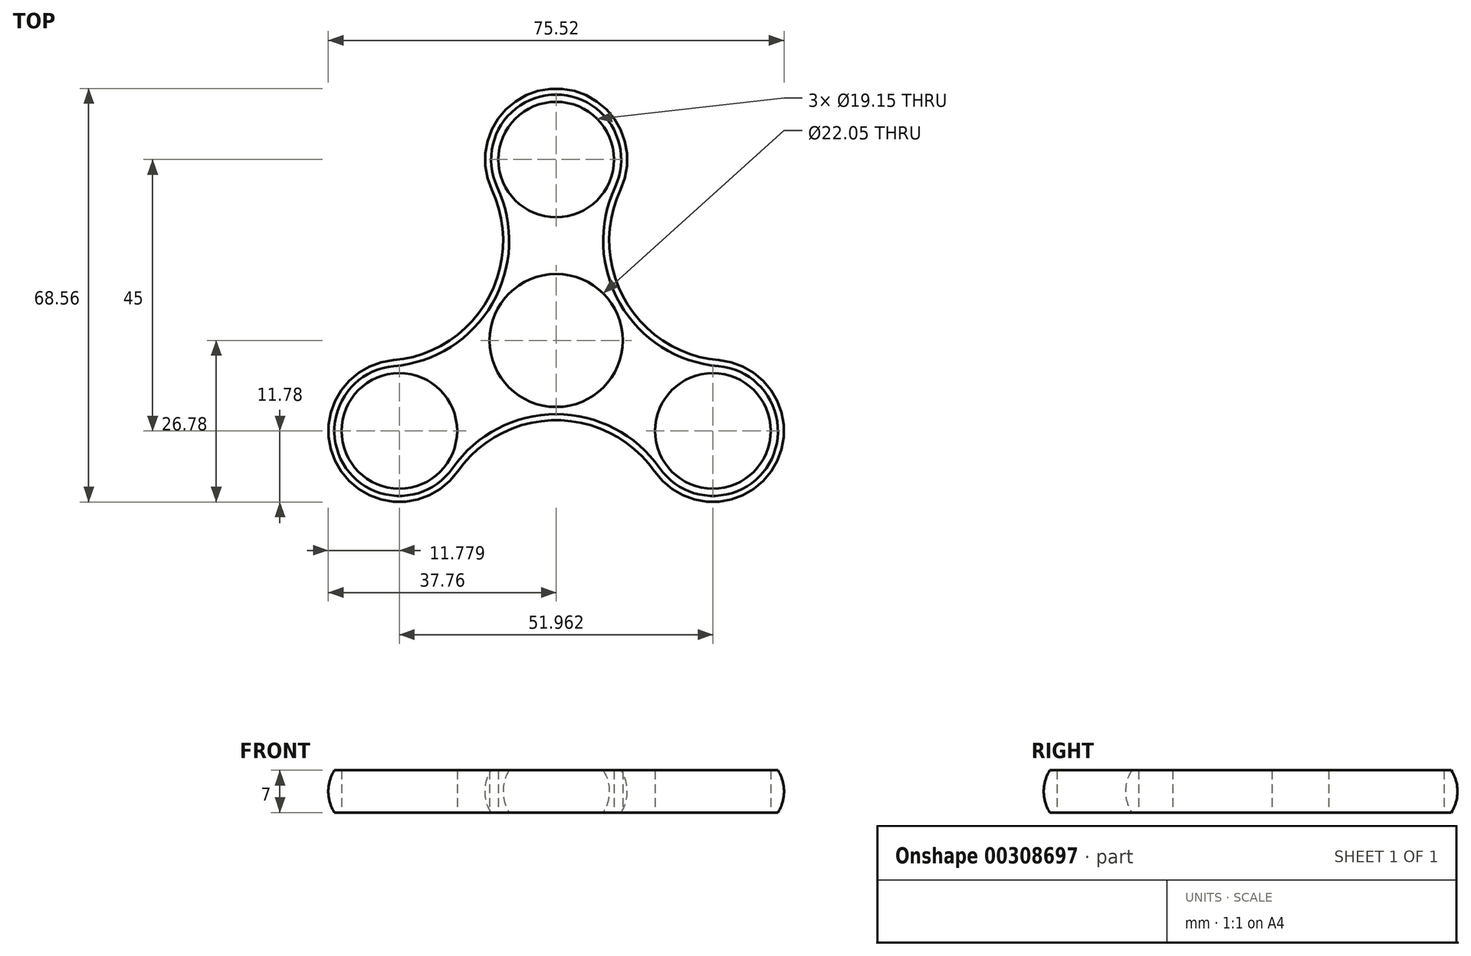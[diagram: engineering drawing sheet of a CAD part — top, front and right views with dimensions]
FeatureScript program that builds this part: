
annotation { "Feature Type Name" : "Feature", "Feature Type Description" : "" }
export const myFeature = defineFeature(function(context is Context, id is Id, definition is map)
    precondition{}
    {
        {
            var Q0;
            Q0=qCreatedBy(makeId("Top.planeOp"),FACE);
            var sketch = newSketch(context, id + "F0", { "sketchPlane" : qUnion([Q0])});
            skCircle(sketch, "E0.cCircle", {"center": v(0, 0) * mm, "radius": 30 * mm, "construction": true});
            skLineSegment(sketch, "E0.0", {"start": v(0, 30) * mm, "end": v(25.98, -15) * mm, "construction": true});
            skLineSegment(sketch, "E0.1", {"start": v(25.98, -15) * mm, "end": v(-25.98, -15) * mm, "construction": true});
            skLineSegment(sketch, "E0.2", {"start": v(-25.98, -15) * mm, "end": v(0, 30) * mm, "construction": true});
            skCircle(sketch, "E1", {"center": v(0, 30) * mm, "radius": 9.57 * mm});
            skCircle(sketch, "E2", {"center": v(25.98, -15) * mm, "radius": 9.57 * mm});
            skCircle(sketch, "E3", {"center": v(-25.98, -15) * mm, "radius": 9.57 * mm});
            skArc(sketch, "E4", {"start": v(-26.9, -4.26) * mm, "mid": v(-10.59, 6.11) * mm, "end": v(-9.76, 25.43) * mm});
            skArc(sketch, "E5", {"start": v(9.76, 25.43) * mm, "mid": v(10.59, 6.11) * mm, "end": v(26.9, -4.26) * mm});
            skArc(sketch, "E6", {"start": v(17.14, -21.17) * mm, "mid": v(0, -12.22) * mm, "end": v(-17.14, -21.17) * mm});
            skCircle(sketch, "E7", {"center": v(0, 0) * mm, "radius": 11.03 * mm});
            skCircle(sketch, "E8", {"center": v(0, 0) * mm, "radius": 12.22 * mm, "construction": true});
            skArc(sketch, "E9", {"start": v(-26.9, -4.26) * mm, "mid": v(-35.31, -20.39) * mm, "end": v(-17.14, -21.17) * mm});
            skArc(sketch, "E10", {"start": v(-17.14, -21.17) * mm, "mid": v(-16.65, -9.61) * mm, "end": v(-26.9, -4.26) * mm, "construction": true});
            skArc(sketch, "E11", {"start": v(17.14, -21.17) * mm, "mid": v(35.31, -20.39) * mm, "end": v(26.9, -4.26) * mm});
            skArc(sketch, "E12", {"start": v(26.9, -4.26) * mm, "mid": v(16.65, -9.61) * mm, "end": v(17.14, -21.17) * mm, "construction": true});
            skArc(sketch, "E13", {"start": v(9.76, 25.43) * mm, "mid": v(0, 40.78) * mm, "end": v(-9.76, 25.43) * mm});
            skArc(sketch, "E14", {"start": v(-9.76, 25.43) * mm, "mid": v(0, 19.22) * mm, "end": v(9.76, 25.43) * mm, "construction": true});
            skPoint(sketch, "E15", {"position": v(-35.31, -20.39) * mm});
            skSolve(sketch);
        }
        {
            var Q0;
            {var subQ0=sQuery(id+"F0.wireOp",EDGE,"E4");Q0=makeQuery(id+"F0.imprint","IMPRINT",FACE,{"disambiguationData":[TD([[makeQuery(id+"F0.imprint","IMPRINT",EDGE,{"derivedFrom":subQ0}),-1.0]])]});}
            var Q1;
            Q1=makeQuery(id+"F0.imprint","IMPRINT",FACE,{"disambiguationData":[TD([[makeQuery(id+"F0.imprint","IMPRINT",EDGE,{"derivedFrom":sQuery(id+"F0.wireOp",EDGE,"E1")}),-1.0]])]});
            var Q2;
            Q2=makeQuery(id+"F0.imprint","IMPRINT",FACE,{"disambiguationData":[TD([[makeQuery(id+"F0.imprint","IMPRINT",EDGE,{"derivedFrom":sQuery(id+"F0.wireOp",EDGE,"E7")}),-1.0]])]});
            var Q3;
            {var subQ0=sQuery(id+"F0.wireOp",EDGE,"E5");var subQ1=sQuery(id+"F0.wireOp",EDGE,"6sLBS57S-66mW-jTRT-EAg4-M7yl9uVLuA44");var subQ2=makeQuery(id+"F0.imprint","INTERSECT",VERTEX,{"derivedFrom":[subQ1,subQ0]});Q3=makeQuery(id+"F0.imprint","IMPRINT",FACE,{"disambiguationData":[TD([[makeQuery(id+"F0.imprint","IMPRINT",EDGE,{"disambiguationData":[TD([[subQ2,-1.0]])],"derivedFrom":subQ1}),-1.0]])]});}
            var Q4;
            Q4=makeQuery(id+"F0.imprint","IMPRINT",FACE,{"disambiguationData":[TD([[makeQuery(id+"F0.imprint","IMPRINT",EDGE,{"derivedFrom":sQuery(id+"F0.wireOp",EDGE,"E2")}),-1.0]])]});
            var Q5;
            Q5=makeQuery(id+"F0.imprint","IMPRINT",FACE,{"disambiguationData":[TD([[makeQuery(id+"F0.imprint","IMPRINT",EDGE,{"derivedFrom":sQuery(id+"F0.wireOp",EDGE,"E3")}),-1.0]])]});
            extrude(context, id + "F1", {"entities" : qUnion([Q0, Q1, Q2, Q3, Q4, Q5]), "endBound" : BoundingType.SYMMETRIC, "depth" : 7 * mm});
        }
        {
            var Q0;
            Q0=sQuery(id+"F0.wireOp",VERTEX,"E14.end");
            var Q1;
            Q1=sQuery(id+"F0.wireOp",EDGE,"E13");
            cPlane(context, id + "F2", {"entities" : qUnion([Q0, Q1]), "cplaneType" : CPlaneType.CURVE_POINT, "offset" : 25 * mm, "width" : 150 * mm, "height" : 150 * mm});
        }
        {
            var Q0;
            Q0=qCreatedBy(id+"F2.planeOp",FACE);
            var sketch = newSketch(context, id + "F3", { "sketchPlane" : qUnion([Q0])});
            skLineSegment(sketch, "E16", {"start": v(23.5, 3.5) * mm, "end": v(23.5, -3.5) * mm});
            skLineSegment(sketch, "E17", {"start": v(1.95, -3.5) * mm, "end": v(1.95, 3.5) * mm});
            skArc(sketch, "E18", {"start": v(1.95, 3.5) * mm, "mid": v(0.95, 0) * mm, "end": v(1.95, -3.5) * mm});
            skLineSegment(sketch, "E19", {"start": v(1.95, 0) * mm, "end": v(0.95, 0) * mm, "construction": true});
            skSolve(sketch);
        }
        {
            var Q0;
            Q0=makeQuery(id+"F3.imprint","IMPRINT",FACE,{"disambiguationData":[TD([[makeQuery(id+"F3.imprint","IMPRINT",EDGE,{"derivedFrom":sQuery(id+"F3.wireOp",EDGE,"E17")}),1.0]])]});
            var Q1;
            Q1=sQuery(id+"F0.wireOp",EDGE,"E13");
            sweep(context, id + "F4", {"operationType" : NewBodyOperationType.ADD, "profiles" : qUnion([Q0]), "path" : qUnion([Q1])});
        }
        {
            var Q0;
            Q0=makeQuery(id+"F4.opSweep","CAP_FACE",FACE,{"disambiguationData":[OSD([sQuery(id+"F0.wireOp",VERTEX,"E13.start"),sQuery(id+"F3.wireOp",EDGE,"E17"),sQuery(id+"F3.wireOp",EDGE,"E18")])],"isStart":true});
            var Q1;
            Q1=sQuery(id+"F0.wireOp",EDGE,"E5");
            var Q2;
            Q2=sQuery(id+"F0.wireOp",EDGE,"E11");
            var Q3;
            Q3=sQuery(id+"F0.wireOp",EDGE,"E6");
            var Q4;
            Q4=sQuery(id+"F0.wireOp",EDGE,"E9");
            var Q5;
            Q5=sQuery(id+"F0.wireOp",EDGE,"E4");
            sweep(context, id + "F5", {"operationType" : NewBodyOperationType.ADD, "profiles" : qUnion([Q0]), "path" : qUnion([Q1, Q2, Q3, Q4, Q5])});
        }
    });
